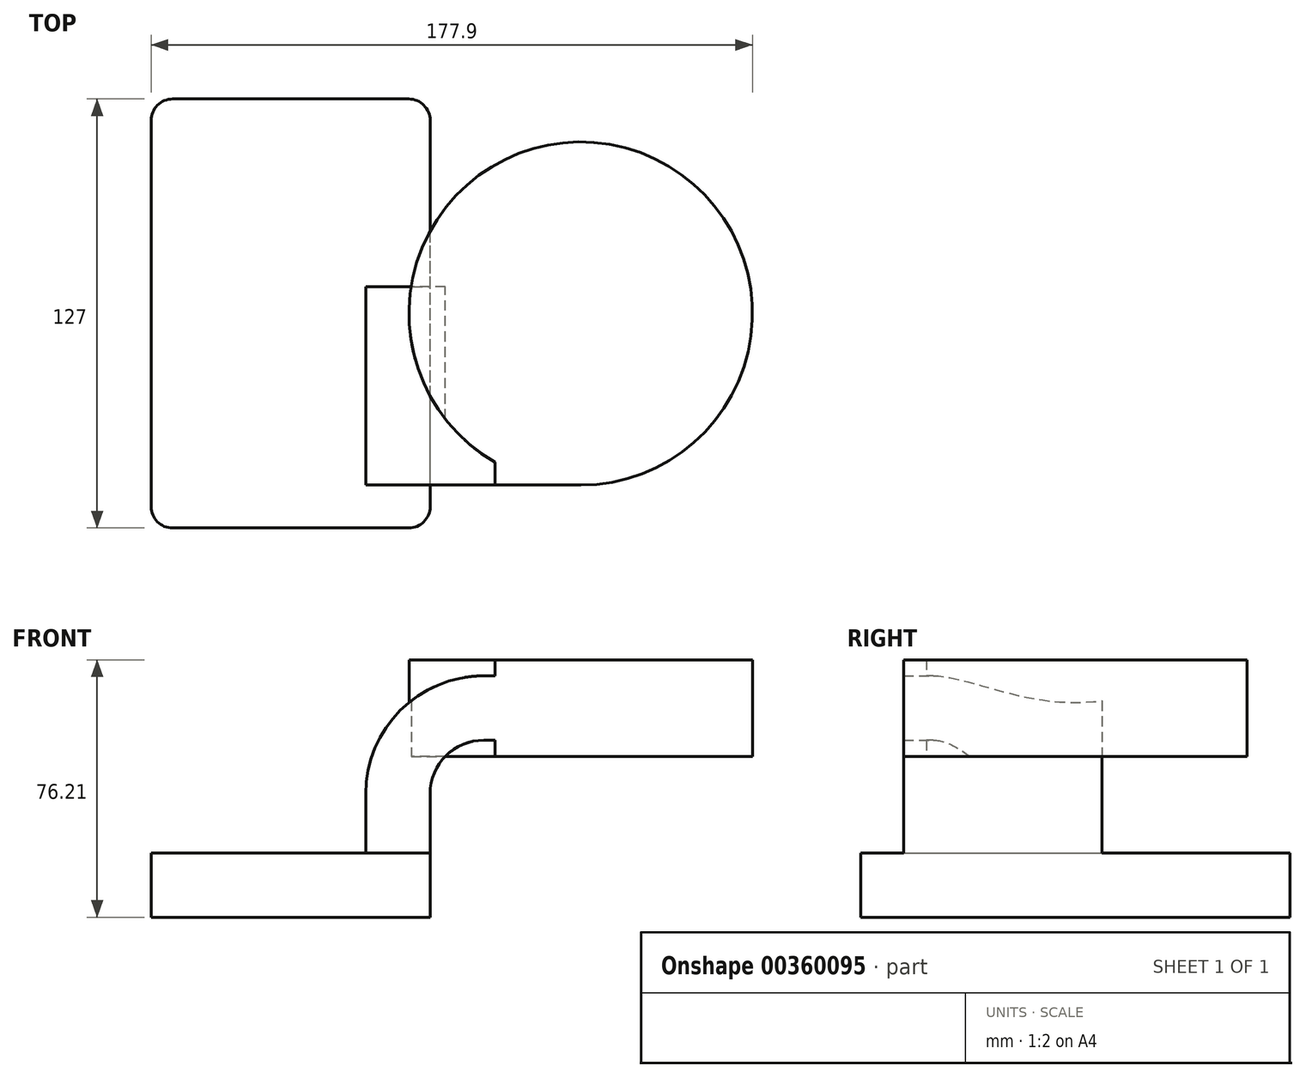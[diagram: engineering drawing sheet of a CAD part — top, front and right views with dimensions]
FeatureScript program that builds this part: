
annotation { "Feature Type Name" : "Feature", "Feature Type Description" : "" }
export const myFeature = defineFeature(function(context is Context, id is Id, definition is map)
    precondition{}
    {
        {
            var Q0;
            Q0=qCreatedBy(makeId("Front.planeOp"),FACE);
            var sketch = newSketch(context, id + "F0", { "sketchPlane" : qUnion([Q0])});
            skLineSegment(sketch, "E0.bottom", {"start": v(-41.28, -9.53) * mm, "end": v(41.28, -9.53) * mm});
            skLineSegment(sketch, "E0.top", {"start": v(-41.28, 9.53) * mm, "end": v(41.28, 9.53) * mm});
            skLineSegment(sketch, "E0.left", {"start": v(-41.28, -9.53) * mm, "end": v(-41.28, 9.53) * mm});
            skLineSegment(sketch, "E0.right", {"start": v(41.28, -9.53) * mm, "end": v(41.28, 9.53) * mm});
            skPoint(sketch, "E0.middle", {"position": v(0, 0) * mm});
            skLineSegment(sketch, "E1.bottom", {"start": v(60.43, 38.1) * mm, "end": v(111.23, 38.1) * mm});
            skLineSegment(sketch, "E1.top", {"start": v(60.43, 66.67) * mm, "end": v(111.23, 66.67) * mm});
            skLineSegment(sketch, "E1.left", {"start": v(60.43, 38.1) * mm, "end": v(60.43, 66.67) * mm});
            skLineSegment(sketch, "E1.right", {"start": v(111.23, 38.1) * mm, "end": v(111.23, 66.67) * mm});
            skPoint(sketch, "E1.middle", {"position": v(85.83, 52.39) * mm});
            skLineSegment(sketch, "E2", {"start": v(41.28, 9.53) * mm, "end": v(41.28, 27) * mm});
            skArc(sketch, "E3", {"start": v(41.27, 27) * mm, "mid": v(45.92, 38.23) * mm, "end": v(57.15, 42.88) * mm});
            skLineSegment(sketch, "E4", {"start": v(57.15, 42.88) * mm, "end": v(83.6, 42.88) * mm});
            skLineSegment(sketch, "E5.0", {"start": v(47.63, 9.53) * mm, "end": v(47.63, 27) * mm});
            skLineSegment(sketch, "E6.0", {"start": v(57.15, 61.93) * mm, "end": v(83.6, 61.93) * mm});
            skArc(sketch, "E6.1", {"start": v(22.23, 27) * mm, "mid": v(32.45, 51.7) * mm, "end": v(57.15, 61.93) * mm});
            skLineSegment(sketch, "E6.2", {"start": v(22.22, 9.53) * mm, "end": v(22.22, 27) * mm});
            skLineSegment(sketch, "E7", {"start": v(85.83, 38.1) * mm, "end": v(85.83, 66.67) * mm});
            skFitSpline(sketch, "E8", {"points": [v(-41.28, 9.52) * mm, v(57.15, 61.93) * mm], "startDerivative": vector(37.6, 119.26) * mm, "endDerivative": vector(96.41, -23.65) * mm});
            skSolve(sketch);
        }
        {
            var Q0;
            Q0=makeQuery(id+"F0.imprint","IMPRINT",FACE,{"disambiguationData":[TD([[makeQuery(id+"F0.imprint","IMPRINT",EDGE,{"derivedFrom":sQuery(id+"F0.wireOp",EDGE,"E0.bottom")}),1.0]])]});
            extrude(context, id + "F1", {"entities" : qUnion([Q0]), "endBound" : BoundingType.SYMMETRIC, "depth" : 127 * mm});
        }
        {
            var Q0;
            {var subQ1=sQuery(id+"F0.wireOp",EDGE,"E2");Q0=makeQuery(id+"F0.imprint","IMPRINT",FACE,{"disambiguationData":[TD([[makeQuery(id+"F0.imprint","IMPRINT",EDGE,{"derivedFrom":subQ1}),1.0]])]});}
            var Q1;
            {var subQ6=sQuery(id+"F0.wireOp",EDGE,"E7");Q1=makeQuery(id+"F0.imprint","IMPRINT",FACE,{"disambiguationData":[TD([[makeQuery(id+"F0.imprint","IMPRINT",EDGE,{"derivedFrom":subQ6}),1.0]])]});}
            extrude(context, id + "F2", {"entities" : qUnion([Q0, Q1]), "operationType" : NewBodyOperationType.ADD, "depth" : 50.8 * mm});
        }
        {
            var Q0;
            Q0=makeQuery(id+"F0.imprint","IMPRINT",FACE,{"disambiguationData":[TD([[makeQuery(id+"F0.imprint","IMPRINT",EDGE,{"derivedFrom":sQuery(id+"F0.wireOp",EDGE,"E6.1")}),1.0]])]});
            extrude(context, id + "F3", {"entities" : qUnion([Q0]), "operationType" : NewBodyOperationType.ADD, "endBound" : BoundingType.SYMMETRIC, "depth" : 15.88 * mm});
        }
        {
            var Q0;
            Q0=makeQuery(id+"F2.opExtrude","SWEPT_FACE",FACE,{"disambiguationData":[OSD([sQuery(id+"F0.wireOp",EDGE,"E7")])]});
            var Q1;
            Q1=sQuery(id+"F0.wireOp",EDGE,"E7");
            revolve(context, id + "F4", {"operationType" : NewBodyOperationType.ADD, "entities" : qUnion([Q0]), "axis" : qUnion([Q1]), "revolveType" : RevolveType.FULL});
        }
        {
            var Q0;
            Q0=makeQuery(id+"F1.opExtrude","CAP_EDGE",EDGE,{"disambiguationData":[OSD([sQuery(id+"F0.wireOp",EDGE,"E0.right")])],"isStart":false});
            var Q1;
            Q1=makeQuery(id+"F1.opExtrude","CAP_EDGE",EDGE,{"disambiguationData":[OSD([sQuery(id+"F0.wireOp",EDGE,"E0.left")])],"isStart":false});
            var Q2;
            Q2=makeQuery(id+"F1.opExtrude","CAP_EDGE",EDGE,{"disambiguationData":[OSD([sQuery(id+"F0.wireOp",EDGE,"E0.right")])],"isStart":true});
            var Q3;
            Q3=makeQuery(id+"F1.opExtrude","CAP_EDGE",EDGE,{"disambiguationData":[OSD([sQuery(id+"F0.wireOp",EDGE,"E0.left")])],"isStart":true});
            fillet(context, id + "F5", {"entities" : qUnion([Q0, Q1, Q2, Q3]), "radius" : 6.35 * mm, "tangentPropagation" : true, "allowEdgeOverflow" : false});
        }
    });
